# Revit family: ledwp-cla-p2_l1500-24_44w-840-md_531000015200_13b4
name_source: partatom
category: Lighting Fixtures
units: mm (PartAtom-declared; Revit-internal decimal feet)

## family parameters
Cut with Voids When Loaded = No
Host = Face
Light Source = No
Part Type = Normal
Room Calculation Point = No
Round Connector Dimension = Use Diameter
Shared = No

## types (1)
- LEDWP-CLA-P2 L1500-24/44W-840-MD (1 x LED, 6600 lm, 4000)
    Apparent Load = 44 VA
    Approval mark = CE, ENEC
    CIE Flux Codes = 49 83 96 98 97
    Color Rendering = 80
    Color Temperature = 4000
    Control Gear = Electronic ballast
    Default Elevation = 1800 mm
    Description = New more sleek classic waterproof solution with clip design . Improved efficacy of 150 lm/W. Optimized diffusor design for more uniform illumination patterns. Wiring from the back or side possible. Supplied with vandal-proof stainless steel ceiling and su
    Frequency = 60 Hz
    Height = 72 mm
    Lamp = 1 x LED
    Lamp Light Flux = 6600 lm
    Lamp count = 1
    Length = 1508 mm
    Luminous efficacy = 145 lm/W
    Manufacturer = OPPLE
    ModVariant = No
    Model = 531000015200
    Number of Poles = 1
    OnlyDefault = Yes
    Power Factor = 1
    Product Name = LEDWP-CLA-P2 L1500-24/44W-840-MD
    Product group = Ceiling / wall-mounted luminaires
    ProductGroupID = 30
    Protection Class = Protection class I
    Protection Degree = IP 65
    RLX_Detail_Level = 1
    RlxData = <blob elided: 249009 chars, md5=3bd9fc3b>
    Socket = socket
    Standby Power = 0 W
    System Light Flux = 6378 lm
    System Power = 44 W
    Type Comments = Product without accessories
    Type Image = web_wp_cla_p2.jpg
    URL = http://relux.com
    VarID = ---
    Voltage = 230 V
    Voltage Range = 220-240 V
    Weight = 0.00 kg
    Width = 78 mm  [stored 0.255906 ft]

note: [stored X ft] marks values corroborated as IEEE doubles in the binary element streams (Revit-internal decimal feet)

## geometry (parser evidence)
native form markers: Sweep x11
no freeform markers — native parametric forms only
